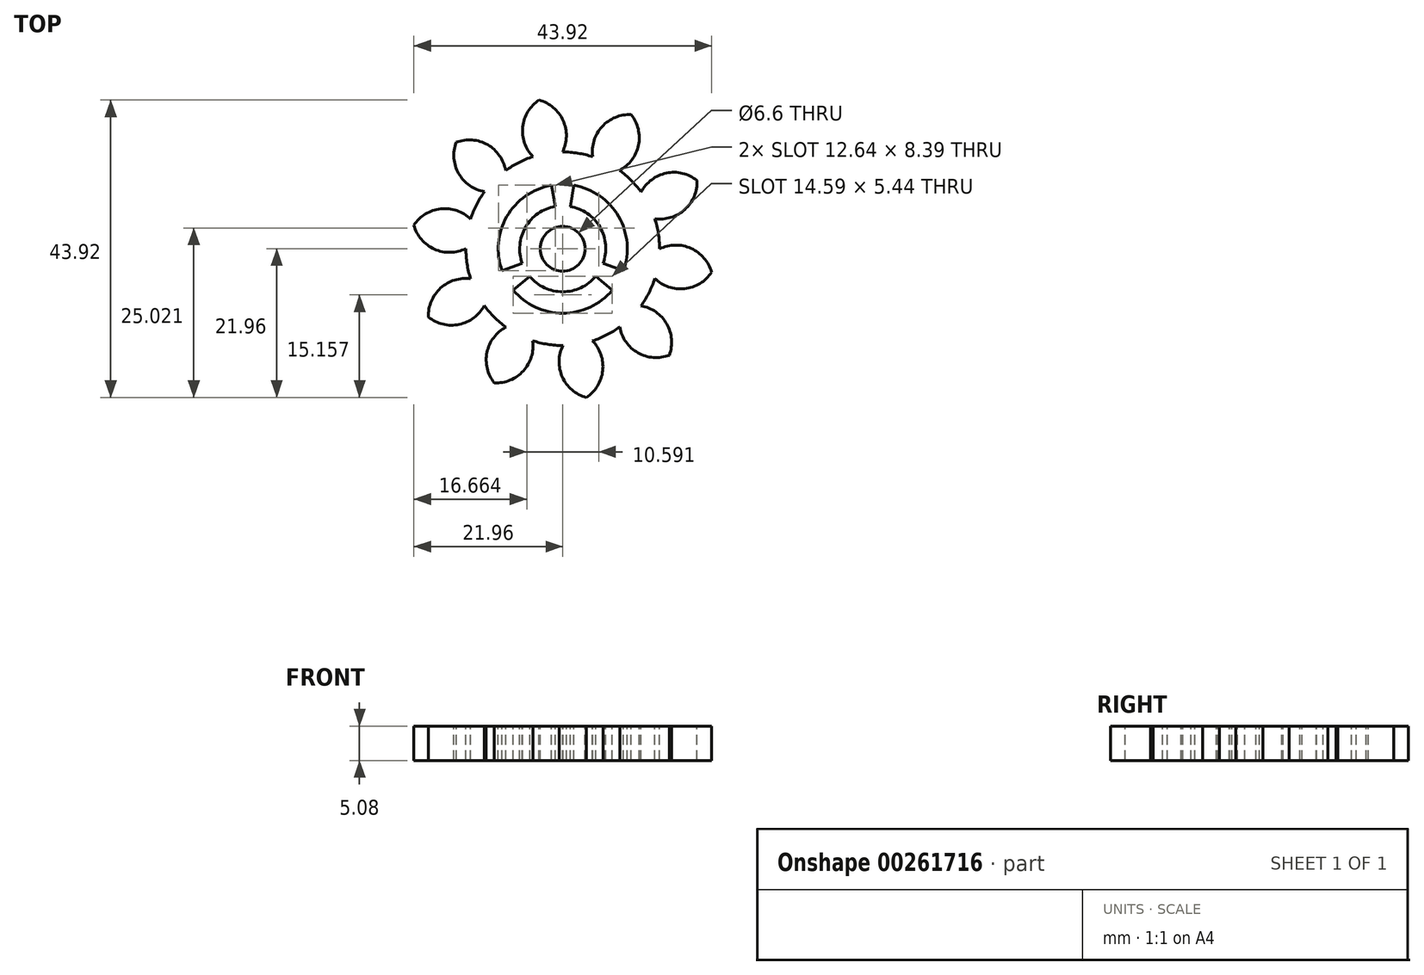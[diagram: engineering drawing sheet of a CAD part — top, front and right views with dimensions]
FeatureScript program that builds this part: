
annotation { "Feature Type Name" : "Feature", "Feature Type Description" : "" }
export const myFeature = defineFeature(function(context is Context, id is Id, definition is map)
    precondition{}
    {
        {
            var Q0;
            Q0=qCreatedBy(makeId("Top.planeOp"),FACE);
            var sketch = newSketch(context, id + "F0", { "sketchPlane" : qUnion([Q0])});
            skCircle(sketch, "E0", {"center": v(0, 0) * mm, "radius": 14.29 * mm});
            skSolve(sketch);
        }
        {
            var Q0;
            Q0=qSketchRegion(id+"F0",true);
            extrude(context, id + "F1", {"entities" : qUnion([Q0]), "depth" : 5.08 * mm});
        }
        {
            var Q0;
            Q0=makeQuery(id+"F1.opExtrude","CAP_FACE",FACE,{"disambiguationData":[OSD([sQuery(id+"F0.wireOp",EDGE,"E0")])],"isStart":false});
            var sketch = newSketch(context, id + "F2", { "sketchPlane" : qUnion([Q0])});
            skCircle(sketch, "E1", {"center": v(0, 0) * mm, "radius": 22.86 * mm, "construction": true});
            skCircle(sketch, "E2", {"center": v(0, 0) * mm, "radius": 19.05 * mm, "construction": true});
            skCircle(sketch, "E3", {"center": v(0, 0) * mm, "radius": 14.29 * mm, "construction": true});
            skLineSegment(sketch, "E4", {"start": v(0, 0) * mm, "end": v(0, 56.9) * mm, "construction": true});
            skLineSegment(sketch, "E5", {"start": v(0, 0) * mm, "end": v(-9.2, 58.1) * mm, "construction": true});
            skLineSegment(sketch, "E6", {"start": v(0, 19.05) * mm, "end": v(-65.71, 19.05) * mm, "construction": true});
            skLineSegment(sketch, "E7", {"start": v(0, 19.05) * mm, "end": v(-58.85, -7.15) * mm, "construction": true});
            skCircle(sketch, "E8", {"center": v(0, 19.05) * mm, "radius": 5.46 * mm, "construction": true});
            skCircle(sketch, "E9", {"center": v(0, 0) * mm, "radius": 17.4 * mm, "construction": true});
            skCircle(sketch, "E10", {"center": v(-4.93, 16.7) * mm, "radius": 5.46 * mm, "construction": true});
            skArc(sketch, "E11", {"start": v(-0.02, 14.29) * mm, "mid": v(0.05, 18.93) * mm, "end": v(-3.48, 21.96) * mm});
            skArc(sketch, "E12.MirrorCS", {"start": v(-4.4, 13.6) * mm, "mid": v(-5.9, 18) * mm, "end": v(-3.48, 21.96) * mm});
            skLineSegment(sketch, "E13", {"start": v(-4.4, 13.6) * mm, "end": v(-0.02, 14.29) * mm});
            skPoint(sketch, "E14.orphan", {"position": v(-0.86, 22.84) * mm});
            skPoint(sketch, "E15.orphan", {"position": v(-6.24, 22) * mm});
            skSolve(sketch);
        }
        {
            var Q0;
            Q0=qSketchRegion(id+"F2",true);
            var Q1;
            Q1=makeQuery(id+"F1.opExtrude","CAP_FACE",FACE,{"disambiguationData":[OSD([sQuery(id+"F0.wireOp",EDGE,"E0")])],"isStart":true});
            extrude(context, id + "F3", {"entities" : qUnion([Q0]), "endBound" : BoundingType.UP_TO_SURFACE, "oppositeDirection" : true, "endBoundEntityFace" : qUnion([Q1]), "depth" : 25.4 * mm});
        }
        {
            var Q0;
            Q0=makeQuery(id+"F3.opExtrude","SWEPT_BODY",BODY,{"disambiguationData":[OSD([sQuery(id+"F2.wireOp",EDGE,"E11"),sQuery(id+"F2.wireOp",EDGE,"E12.MirrorCS"),sQuery(id+"F2.wireOp",EDGE,"E13")])]});
            var Q1;
            Q1=makeQuery(id+"F1.opExtrude","CAP_EDGE",EDGE,{"disambiguationData":[OSD([sQuery(id+"F0.wireOp",EDGE,"E0")])],"isStart":false});
            circularPattern(context, id + "F4", {"operationType" : NewBodyOperationType.ADD, "entities" : qUnion([Q0]), "axis" : qUnion([Q1]), "angle" : 360 * degree, "instanceCount" : 10, "equalSpace" : true});
        }
        {
            var Q0;
            {var subQ0=makeQuery(id+"F3.opExtrude","CAP_FACE",FACE,{"disambiguationData":[OSD([sQuery(id+"F2.wireOp",EDGE,"E11"),sQuery(id+"F2.wireOp",EDGE,"E12.MirrorCS"),sQuery(id+"F2.wireOp",EDGE,"E13")])],"isStart":true});Q0=makeQuery(id+"F4.boolean.opBoolean","MERGE",FACE,{"derivedFrom":[makeQuery(id+"F1.opExtrude","CAP_FACE",FACE,{"disambiguationData":[OSD([sQuery(id+"F0.wireOp",EDGE,"E0")])],"isStart":false}),subQ0,makeQuery(id+"F4.opPattern","COPY",FACE,{"derivedFrom":subQ0,"instanceName":"1"}),makeQuery(id+"F4.opPattern","COPY",FACE,{"derivedFrom":subQ0,"instanceName":"2"}),makeQuery(id+"F4.opPattern","COPY",FACE,{"derivedFrom":subQ0,"instanceName":"3"}),makeQuery(id+"F4.opPattern","COPY",FACE,{"derivedFrom":subQ0,"instanceName":"4"}),makeQuery(id+"F4.opPattern","COPY",FACE,{"derivedFrom":subQ0,"instanceName":"5"}),makeQuery(id+"F4.opPattern","COPY",FACE,{"derivedFrom":subQ0,"instanceName":"6"}),makeQuery(id+"F4.opPattern","COPY",FACE,{"derivedFrom":subQ0,"instanceName":"7"}),makeQuery(id+"F4.opPattern","COPY",FACE,{"derivedFrom":subQ0,"instanceName":"8"}),makeQuery(id+"F4.opPattern","COPY",FACE,{"derivedFrom":subQ0,"instanceName":"9"})]});}
            var sketch = newSketch(context, id + "F5", { "sketchPlane" : qUnion([Q0])});
            skCircle(sketch, "E16", {"center": v(0, 0) * mm, "radius": 9.53 * mm});
            skSolve(sketch);
        }
        {
            var Q0;
            Q0=qSketchRegion(id+"F5",true);
            extrude(context, id + "F6", {"entities" : qUnion([Q0]), "operationType" : NewBodyOperationType.REMOVE, "endBound" : BoundingType.THROUGH_ALL, "oppositeDirection" : true, "depth" : 25.4 * mm});
        }
        {
            var Q0;
            Q0=qSketchRegion(id+"F5",true);
            extrude(context, id + "F7", {"entities" : qUnion([Q0]), "operationType" : NewBodyOperationType.REMOVE, "endBound" : BoundingType.THROUGH_ALL, "oppositeDirection" : true, "depth" : 25.4 * mm});
        }
        {
            var Q0;
            {var subQ0=makeQuery(id+"F3.opExtrude","CAP_FACE",FACE,{"disambiguationData":[OSD([sQuery(id+"F2.wireOp",EDGE,"E11"),sQuery(id+"F2.wireOp",EDGE,"E12.MirrorCS"),sQuery(id+"F2.wireOp",EDGE,"E13")])],"isStart":true});Q0=makeQuery(id+"F4.boolean.opBoolean","MERGE",FACE,{"derivedFrom":[makeQuery(id+"F1.opExtrude","CAP_FACE",FACE,{"disambiguationData":[OSD([sQuery(id+"F0.wireOp",EDGE,"E0")])],"isStart":false}),subQ0,makeQuery(id+"F4.opPattern","COPY",FACE,{"derivedFrom":subQ0,"instanceName":"1"}),makeQuery(id+"F4.opPattern","COPY",FACE,{"derivedFrom":subQ0,"instanceName":"2"}),makeQuery(id+"F4.opPattern","COPY",FACE,{"derivedFrom":subQ0,"instanceName":"3"}),makeQuery(id+"F4.opPattern","COPY",FACE,{"derivedFrom":subQ0,"instanceName":"4"}),makeQuery(id+"F4.opPattern","COPY",FACE,{"derivedFrom":subQ0,"instanceName":"5"}),makeQuery(id+"F4.opPattern","COPY",FACE,{"derivedFrom":subQ0,"instanceName":"6"}),makeQuery(id+"F4.opPattern","COPY",FACE,{"derivedFrom":subQ0,"instanceName":"7"}),makeQuery(id+"F4.opPattern","COPY",FACE,{"derivedFrom":subQ0,"instanceName":"8"}),makeQuery(id+"F4.opPattern","COPY",FACE,{"derivedFrom":subQ0,"instanceName":"9"})]});}
            var sketch = newSketch(context, id + "F8", { "sketchPlane" : qUnion([Q0])});
            skArc(sketch, "E17", {"start": v(-1.1, 6.25) * mm, "mid": v(0, -6.35) * mm, "end": v(1.1, 6.25) * mm});
            skLineSegment(sketch, "E18", {"start": v(-1.1, 6.25) * mm, "end": v(-1.65, 9.38) * mm});
            skArc(sketch, "E19", {"start": v(1.65, 9.38) * mm, "mid": v(0, 9.53) * mm, "end": v(-1.65, 9.38) * mm});
            skLineSegment(sketch, "E20", {"start": v(1.65, 9.38) * mm, "end": v(1.1, 6.25) * mm});
            skSolve(sketch);
        }
        {
            var Q0;
            Q0=qSketchRegion(id+"F8",true);
            var Q1;
            {var subQ0=makeQuery(id+"F3.opExtrude","CAP_FACE",FACE,{"disambiguationData":[OSD([sQuery(id+"F2.wireOp",EDGE,"E11"),sQuery(id+"F2.wireOp",EDGE,"E12.MirrorCS"),sQuery(id+"F2.wireOp",EDGE,"E13")])],"isStart":false});Q1=makeQuery(id+"F4.boolean.opBoolean","MERGE",FACE,{"derivedFrom":[makeQuery(id+"F1.opExtrude","CAP_FACE",FACE,{"disambiguationData":[OSD([sQuery(id+"F0.wireOp",EDGE,"E0")])],"isStart":true}),subQ0,makeQuery(id+"F4.opPattern","COPY",FACE,{"derivedFrom":subQ0,"instanceName":"1"}),makeQuery(id+"F4.opPattern","COPY",FACE,{"derivedFrom":subQ0,"instanceName":"2"}),makeQuery(id+"F4.opPattern","COPY",FACE,{"derivedFrom":subQ0,"instanceName":"3"}),makeQuery(id+"F4.opPattern","COPY",FACE,{"derivedFrom":subQ0,"instanceName":"4"}),makeQuery(id+"F4.opPattern","COPY",FACE,{"derivedFrom":subQ0,"instanceName":"5"}),makeQuery(id+"F4.opPattern","COPY",FACE,{"derivedFrom":subQ0,"instanceName":"6"}),makeQuery(id+"F4.opPattern","COPY",FACE,{"derivedFrom":subQ0,"instanceName":"7"}),makeQuery(id+"F4.opPattern","COPY",FACE,{"derivedFrom":subQ0,"instanceName":"8"}),makeQuery(id+"F4.opPattern","COPY",FACE,{"derivedFrom":subQ0,"instanceName":"9"})]});}
            extrude(context, id + "F9", {"entities" : qUnion([Q0]), "endBound" : BoundingType.UP_TO_SURFACE, "oppositeDirection" : true, "endBoundEntityFace" : qUnion([Q1]), "depth" : 25.4 * mm});
        }
        {
            var Q0;
            Q0=makeQuery(id+"F9.opExtrude","SWEPT_BODY",BODY,{"disambiguationData":[OSD([sQuery(id+"F8.wireOp",EDGE,"E17"),sQuery(id+"F8.wireOp",EDGE,"E18"),sQuery(id+"F8.wireOp",EDGE,"E19"),sQuery(id+"F8.wireOp",EDGE,"E20")])]});
            var Q1;
            Q1=makeQuery(id+"F9.opExtrude","SWEPT_FACE",FACE,{"disambiguationData":[OSD([sQuery(id+"F8.wireOp",EDGE,"E17")])]});
            circularPattern(context, id + "F10", {"operationType" : NewBodyOperationType.ADD, "entities" : qUnion([Q0]), "axis" : qUnion([Q1]), "angle" : 360 * degree, "instanceCount" : 3, "equalSpace" : true});
        }
        {
            var Q0;
            {var subQ0=makeQuery(id+"F9.opExtrude","CAP_FACE",FACE,{"disambiguationData":[OSD([sQuery(id+"F8.wireOp",EDGE,"E17"),sQuery(id+"F8.wireOp",EDGE,"E18"),sQuery(id+"F8.wireOp",EDGE,"E19"),sQuery(id+"F8.wireOp",EDGE,"E20")])],"isStart":true});var subQ1=makeQuery(id+"F3.opExtrude","CAP_FACE",FACE,{"disambiguationData":[OSD([sQuery(id+"F2.wireOp",EDGE,"E11"),sQuery(id+"F2.wireOp",EDGE,"E12.MirrorCS"),sQuery(id+"F2.wireOp",EDGE,"E13")])],"isStart":true});Q0=makeQuery(id+"F10.boolean.opBoolean","MERGE",FACE,{"derivedFrom":[makeQuery(id+"F4.boolean.opBoolean","MERGE",FACE,{"derivedFrom":[makeQuery(id+"F1.opExtrude","CAP_FACE",FACE,{"disambiguationData":[OSD([sQuery(id+"F0.wireOp",EDGE,"E0")])],"isStart":false}),subQ1,makeQuery(id+"F4.opPattern","COPY",FACE,{"derivedFrom":subQ1,"instanceName":"1"}),makeQuery(id+"F4.opPattern","COPY",FACE,{"derivedFrom":subQ1,"instanceName":"2"}),makeQuery(id+"F4.opPattern","COPY",FACE,{"derivedFrom":subQ1,"instanceName":"3"}),makeQuery(id+"F4.opPattern","COPY",FACE,{"derivedFrom":subQ1,"instanceName":"4"}),makeQuery(id+"F4.opPattern","COPY",FACE,{"derivedFrom":subQ1,"instanceName":"5"}),makeQuery(id+"F4.opPattern","COPY",FACE,{"derivedFrom":subQ1,"instanceName":"6"}),makeQuery(id+"F4.opPattern","COPY",FACE,{"derivedFrom":subQ1,"instanceName":"7"}),makeQuery(id+"F4.opPattern","COPY",FACE,{"derivedFrom":subQ1,"instanceName":"8"}),makeQuery(id+"F4.opPattern","COPY",FACE,{"derivedFrom":subQ1,"instanceName":"9"})]}),subQ0,makeQuery(id+"F10.opPattern","COPY",FACE,{"derivedFrom":subQ0,"instanceName":"1"}),makeQuery(id+"F10.opPattern","COPY",FACE,{"derivedFrom":subQ0,"instanceName":"2"})]});}
            var sketch = newSketch(context, id + "F11", { "sketchPlane" : qUnion([Q0])});
            skCircle(sketch, "E21", {"center": v(0, 0) * mm, "radius": 3.3 * mm});
            skSolve(sketch);
        }
        {
            var Q0;
            Q0=qSketchRegion(id+"F11",true);
            extrude(context, id + "F12", {"entities" : qUnion([Q0]), "operationType" : NewBodyOperationType.REMOVE, "endBound" : BoundingType.THROUGH_ALL, "oppositeDirection" : true, "depth" : 25.4 * mm});
        }
    });
